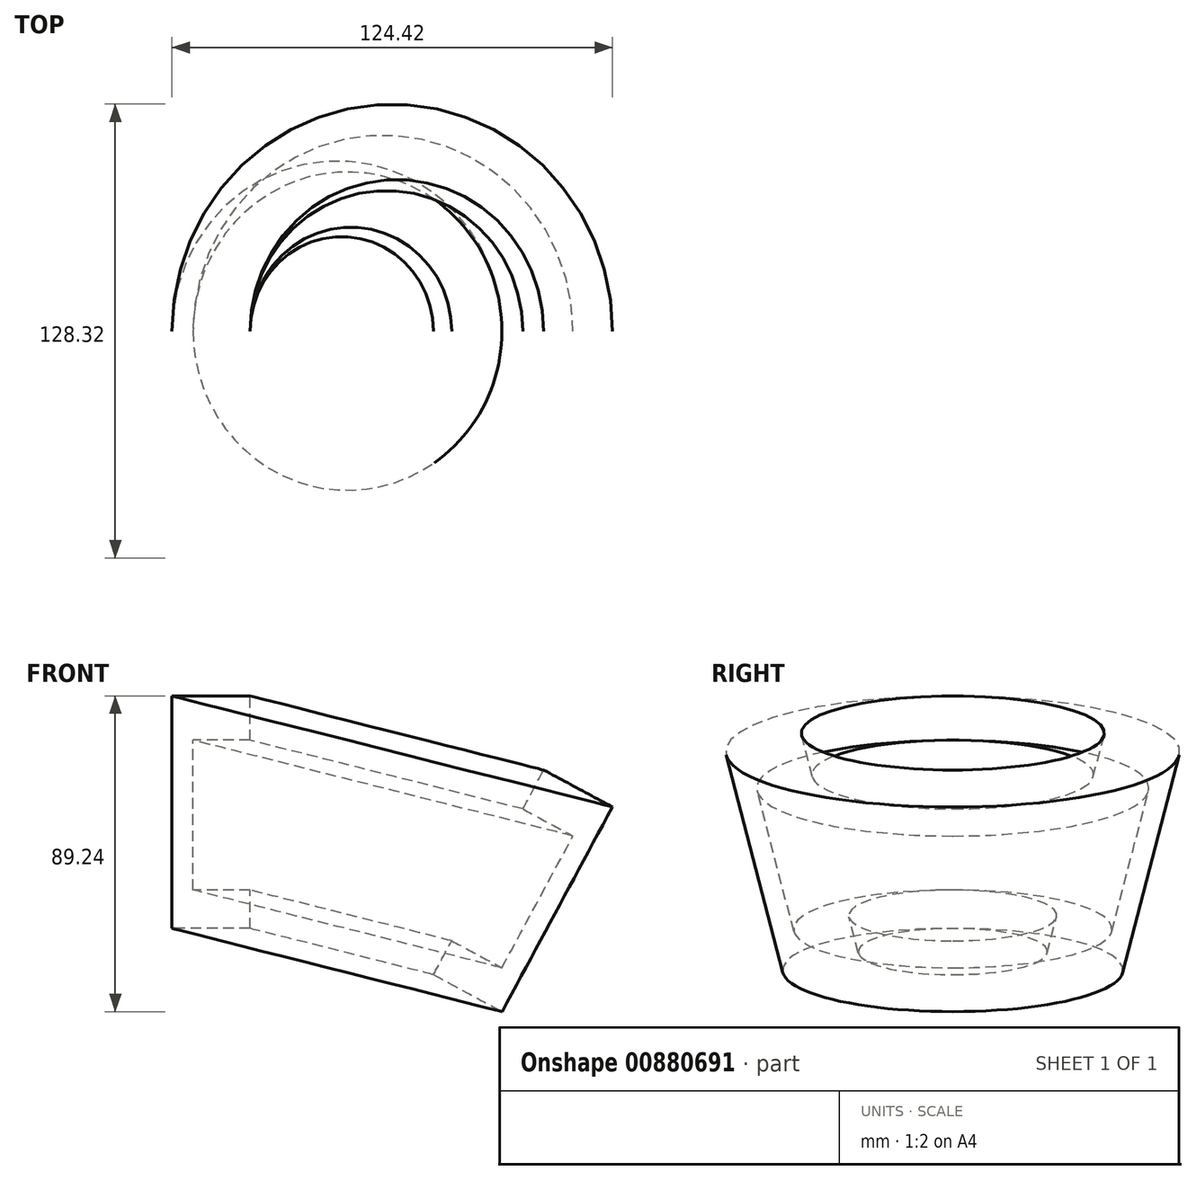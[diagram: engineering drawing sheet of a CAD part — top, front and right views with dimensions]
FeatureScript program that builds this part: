
annotation { "Feature Type Name" : "Feature", "Feature Type Description" : "" }
export const myFeature = defineFeature(function(context is Context, id is Id, definition is map)
    precondition{}
    {
        {
            var Q0;
            Q0=qCreatedBy(makeId("Front.planeOp"),FACE);
            var sketch = newSketch(context, id + "F0", { "sketchPlane" : qUnion([Q0])});
            skLineSegment(sketch, "E0.bottom", {"start": v(-31.78, 40.63) * mm, "end": v(-9.74, 40.63) * mm});
            skLineSegment(sketch, "E0.top", {"start": v(-31.78, -25.09) * mm, "end": v(-9.74, -25.09) * mm});
            skLineSegment(sketch, "E0.left", {"start": v(-31.78, 40.63) * mm, "end": v(-31.78, -25.09) * mm});
            skLineSegment(sketch, "E0.right", {"start": v(-9.74, 40.63) * mm, "end": v(-9.74, 28.12) * mm});
            skLineSegment(sketch, "E1", {"start": v(28.03, 15.4) * mm, "end": v(16.4, -30.67) * mm, "construction": true});
            skLineSegment(sketch, "E2.bottom", {"start": v(-9.74, 28.12) * mm, "end": v(-25.84, 28.12) * mm});
            skLineSegment(sketch, "E2.top", {"start": v(-9.74, -14.22) * mm, "end": v(-25.84, -14.22) * mm});
            skLineSegment(sketch, "E2.right", {"start": v(-25.84, 28.12) * mm, "end": v(-25.84, -14.22) * mm});
            skLineSegment(sketch, "E3.trimOffspring", {"start": v(-9.74, -14.22) * mm, "end": v(-9.74, -25.09) * mm});
            skSolve(sketch);
        }
        {
            var Q0;
            Q0=makeQuery(id+"F0.imprint","IMPRINT",FACE,{"disambiguationData":[TD([[makeQuery(id+"F0.imprint","IMPRINT",EDGE,{"derivedFrom":sQuery(id+"F0.wireOp",EDGE,"E0.bottom")}),-1.0]])]});
            var Q1;
            Q1=sQuery(id+"F0.wireOp",EDGE,"E1");
            revolve(context, id + "F1", {"surfaceOperationType" : NewSurfaceOperationType.NEW, "entities" : qUnion([Q0]), "axis" : qUnion([Q1]), "revolveType" : RevolveType.FULL});
        }
    });
